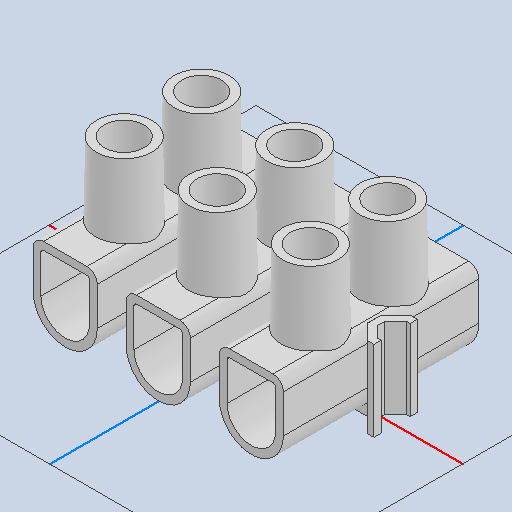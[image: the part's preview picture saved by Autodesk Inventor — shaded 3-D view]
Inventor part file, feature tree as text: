
AUTODESK INVENTOR PART (.ipt)
format: ipt  version: 2022 (Build 260153000, 153)  size: 492,032 bytes
history: native  units: mm
features: other x13, fillet x1
ambient origin geometry x8: Origin, YZ Plane, XZ Plane, XY Plane, X Axis, Y Axis, Z Axis, Center Point
bodies: Body1 (feature_tree), Body2 (feature_tree), Body3 (feature_tree), Body4 (feature_tree), Body5 (feature_tree), Body6 (feature_tree), Body7 (feature_tree)
feature tree (14):
  other  "Твердое тело1"
  other  "Твердое тело2"
  other  "Твердое тело3"
  other  "Твердое тело4"
  other  "Твердое тело5"
  other  "Твердое тело6"
  other  "Твердое тело7"
  other  "Boss-Extrude4"
  fillet  "Fillet1"  [1 undecoded]
  other  "LPattern3[1]"
  other  "LPattern3[2]"
  other  "LPattern3[3]"
  other  "LPattern3[4]"
  other  "LPattern3[5]"
note: 1 required parameter value undecoded (feature->parameter linkage not recoverable at this tier; creation-order binding heuristic only, values carry confidence <= 0.55)
